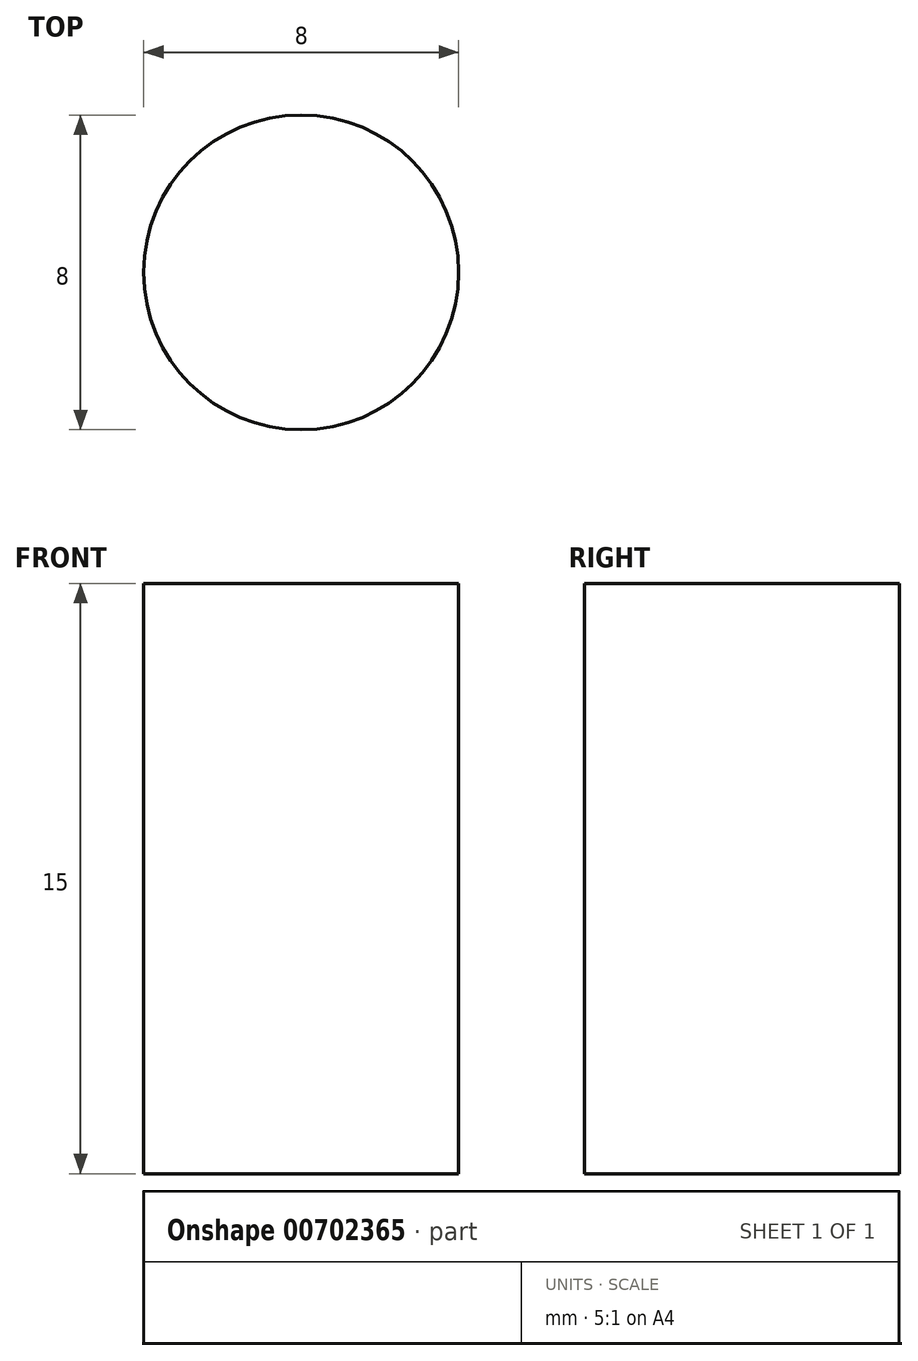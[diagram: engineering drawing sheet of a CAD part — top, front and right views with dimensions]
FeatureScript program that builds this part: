
annotation { "Feature Type Name" : "Feature", "Feature Type Description" : "" }
export const myFeature = defineFeature(function(context is Context, id is Id, definition is map)
    precondition{}
    {
        {
            var Q0;
            Q0=qCreatedBy(makeId("Top.planeOp"),FACE);
            var sketch = newSketch(context, id + "F0", { "sketchPlane" : qUnion([Q0])});
            skCircle(sketch, "E0", {"center": v(0, 0) * mm, "radius": 4 * mm});
            skSolve(sketch);
        }
        {
            var Q0;
            Q0=makeQuery(id+"F0.imprint","IMPRINT",FACE,{"disambiguationData":[TD([[makeQuery(id+"F0.imprint","IMPRINT",EDGE,{"derivedFrom":sQuery(id+"F0.wireOp",EDGE,"E0")}),1.0]])]});
            extrude(context, id + "F1", {"entities" : qUnion([Q0]), "depth" : 15 * mm, "offsetDistance" : 25 * mm});
        }
    });
